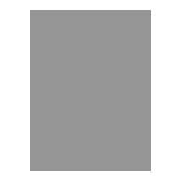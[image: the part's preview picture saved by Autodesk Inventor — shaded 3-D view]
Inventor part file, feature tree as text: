
AUTODESK INVENTOR PART (.ipt)
format: ipt  version: 2019.4 (Build 234330000, 330)  size: 113,152 bytes
history: native  units: mm (DEFAULTED — no unit token found)
features: other x4, plane x3, split x2, sketch x2
ambient origin geometry x8: Origin, YZ Plane, XZ Plane, XY Plane, X Axis, Y Axis, Z Axis, Center Point
bodies: Solid1 (feature_tree), Body (feature_tree)
feature tree (11):
  parser-record x1  (decoder bookkeeping rows leaked as tree rows — omitted from the tree; the rows remain in map.json)
  other  "Driven Length"
  other  "Start plane"
  other  "End plane"
  plane  "Work Plane4"
  split  "Split1"
  plane  "Work Plane5"
  split  "Split2"
  sketch  "Sketch3"  dims[d0=12.7mm]
  plane  "Work Plane3"
  sketch  "Sketch4"  dims[d1=12.7mm d2=190.5mm d3=0.0mm d4=6.35mm d5=6.35mm d6=6.35mm d7=196.85mm d8=90.0deg d9=190.5mm]
